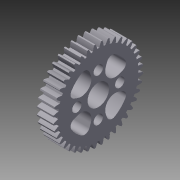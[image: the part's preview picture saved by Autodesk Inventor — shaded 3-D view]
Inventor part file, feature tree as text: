
AUTODESK INVENTOR PART (.ipt)
format: ipt  version: 2012 (Build 160160000, 160)  size: 350,720 bytes
history: native  units: in
note: dims shown in document units (in); Inventor stores cm internally (conversion verified against a paired STEP export)
features: imported_body x1, extrude x1, fillet x1, pattern_circular x1, sketch x1
ambient origin geometry x8: Origin, YZ Plane, XZ Plane, XY Plane, X Axis, Y Axis, Z Axis, Center Point
bodies: Solid1 (feature_tree)
feature tree (5):
  imported_body  "Base1"
  extrude  "Extrusion1"  Depth=0.1374in
  fillet  "Fillet1"  Radius=0.1374in
  pattern_circular  "Circular Pattern1"  [2 undecoded]
  sketch  "Sketch1"  dims[d0=0.125in d1=0.1374in d2=0.1374in d3=0.15in d4=0.3937in d5=0.0in d6=0.0787in d7=1.5748in d8=360.0deg]
note: 2 required parameter values undecoded (feature->parameter linkage not recoverable at this tier; creation-order binding heuristic only, values carry confidence <= 0.55)
